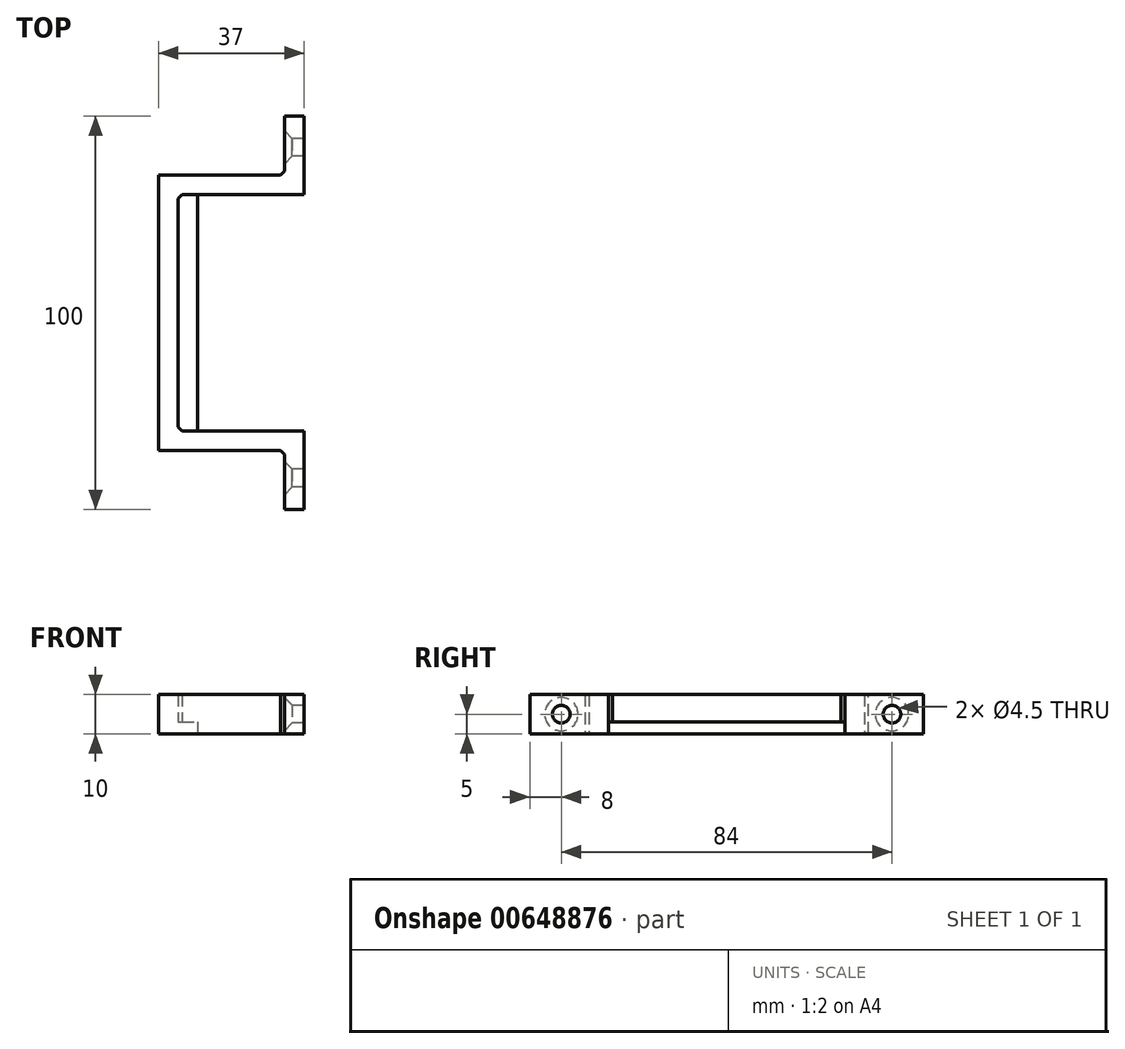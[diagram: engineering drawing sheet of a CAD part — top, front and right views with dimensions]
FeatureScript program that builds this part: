
annotation { "Feature Type Name" : "Feature", "Feature Type Description" : "" }
export const myFeature = defineFeature(function(context is Context, id is Id, definition is map)
    precondition{}
    {
        {
            var Q0;
            Q0=qCreatedBy(makeId("Top.planeOp"),FACE);
            var sketch = newSketch(context, id + "F0", { "sketchPlane" : qUnion([Q0])});
            skLineSegment(sketch, "E0", {"start": v(-30.24, 0) * mm, "end": v(66.75, 0) * mm, "construction": true});
            skLineSegment(sketch, "E1", {"start": v(0, 0) * mm, "end": v(0, 30) * mm});
            skLineSegment(sketch, "E2", {"start": v(0, 30) * mm, "end": v(32, 30) * mm});
            skLineSegment(sketch, "E3", {"start": v(32, 30) * mm, "end": v(32, 50) * mm});
            skLineSegment(sketch, "E4", {"start": v(32, 50) * mm, "end": v(27, 50) * mm});
            skLineSegment(sketch, "E5", {"start": v(27, 50) * mm, "end": v(27, 35) * mm});
            skLineSegment(sketch, "E6", {"start": v(27, 35) * mm, "end": v(-5, 35) * mm});
            skLineSegment(sketch, "E7", {"start": v(-5, 35) * mm, "end": v(-5, 0) * mm});
            skLineSegment(sketch, "E8.MirrorCS", {"start": v(-5, -35) * mm, "end": v(-5, 0) * mm});
            skLineSegment(sketch, "E9.MirrorCS", {"start": v(0, 0) * mm, "end": v(0, -30) * mm});
            skLineSegment(sketch, "E10.MirrorCS", {"start": v(27, -35) * mm, "end": v(-5, -35) * mm});
            skLineSegment(sketch, "E11.MirrorCS", {"start": v(0, -30) * mm, "end": v(32, -30) * mm});
            skLineSegment(sketch, "E12.MirrorCS", {"start": v(27, -50) * mm, "end": v(27, -35) * mm});
            skLineSegment(sketch, "E13.MirrorCS", {"start": v(32, -30) * mm, "end": v(32, -50) * mm});
            skLineSegment(sketch, "E14.MirrorCS", {"start": v(32, -50) * mm, "end": v(27, -50) * mm});
            skLineSegment(sketch, "E15", {"start": v(5, 30) * mm, "end": v(5, -30) * mm});
            skSolve(sketch);
        }
        {
            var Q0;
            {var subQ0=sQuery(id+"F0.wireOp",EDGE,"E3");Q0=makeQuery(id+"F0.imprint","IMPRINT",FACE,{"disambiguationData":[TD([[makeQuery(id+"F0.imprint","IMPRINT",EDGE,{"derivedFrom":subQ0}),1.0]])]});}
            extrude(context, id + "F1", {"entities" : qUnion([Q0]), "depth" : 10 * mm, "offsetDistance" : 25 * mm});
        }
        {
            var Q0;
            Q0=makeQuery(id+"F1.opExtrude","SWEPT_EDGE",EDGE,{"disambiguationData":[OSD([sQuery(id+"F0.wireOp",EDGE,"E9.MirrorCS"),sQuery(id+"F0.wireOp",EDGE,"E11.MirrorCS")])]});
            var Q1;
            Q1=makeQuery(id+"F1.opExtrude","SWEPT_EDGE",EDGE,{"disambiguationData":[OSD([sQuery(id+"F0.wireOp",EDGE,"E10.MirrorCS"),sQuery(id+"F0.wireOp",EDGE,"E12.MirrorCS")])]});
            var Q2;
            Q2=makeQuery(id+"F1.opExtrude","SWEPT_EDGE",EDGE,{"disambiguationData":[OSD([sQuery(id+"F0.wireOp",EDGE,"E1"),sQuery(id+"F0.wireOp",EDGE,"E2")])]});
            var Q3;
            Q3=makeQuery(id+"F1.opExtrude","SWEPT_EDGE",EDGE,{"disambiguationData":[OSD([sQuery(id+"F0.wireOp",EDGE,"E5"),sQuery(id+"F0.wireOp",EDGE,"E6")])]});
            chamfer(context, id + "F2", {"entities" : qUnion([Q0, Q1, Q2, Q3]), "width" : 1 * mm, "tangentPropagation" : true});
        }
        {
            var Q0;
            Q0=makeQuery(id+"F1.opExtrude","SWEPT_FACE",FACE,{"disambiguationData":[OSD([sQuery(id+"F0.wireOp",EDGE,"E12.MirrorCS")])]});
            cPlane(context, id + "F3", {"entities" : qUnion([Q0]), "cplaneType" : CPlaneType.OFFSET, "offset" : 0 * mm, "width" : 150 * mm, "height" : 150 * mm});
        }
        {
            var Q0;
            Q0=qCreatedBy(id+"F3.planeOp",FACE);
            var sketch = newSketch(context, id + "F4", { "sketchPlane" : qUnion([Q0])});
            skLineSegment(sketch, "E16", {"start": v(55.78, 5) * mm, "end": v(-61.85, 5) * mm, "construction": true});
            skPoint(sketch, "E17", {"position": v(42, 5) * mm});
            skPoint(sketch, "E18", {"position": v(-42, 5) * mm});
            skSolve(sketch);
        }
        {
            var Q0;
            Q0=sQuery(id+"F4.wireOp",VERTEX,"E17");
            var Q1;
            Q1=sQuery(id+"F4.wireOp",VERTEX,"E18");
            var Q2;
            Q2=makeQuery(id+"F1.opExtrude","SWEPT_BODY",BODY,{"disambiguationData":[OSD([sQuery(id+"F0.wireOp",EDGE,"E1"),sQuery(id+"F0.wireOp",EDGE,"E2"),sQuery(id+"F0.wireOp",EDGE,"E3"),sQuery(id+"F0.wireOp",EDGE,"E4"),sQuery(id+"F0.wireOp",EDGE,"E5"),sQuery(id+"F0.wireOp",EDGE,"E6"),sQuery(id+"F0.wireOp",EDGE,"E7"),sQuery(id+"F0.wireOp",EDGE,"E8.MirrorCS"),sQuery(id+"F0.wireOp",EDGE,"E9.MirrorCS"),sQuery(id+"F0.wireOp",EDGE,"E10.MirrorCS"),sQuery(id+"F0.wireOp",EDGE,"E11.MirrorCS"),sQuery(id+"F0.wireOp",EDGE,"E12.MirrorCS"),sQuery(id+"F0.wireOp",EDGE,"E13.MirrorCS"),sQuery(id+"F0.wireOp",EDGE,"E14.MirrorCS")])]});
            hole(context, id + "F5", {"style" : HoleStyle.C_SINK, "endStyle" : HoleEndStyle.THROUGH, "holeDiameter" : 4.5 * mm, "cSinkDiameter" : 8.5 * mm, "cSinkAngle" : 90 * degree, "majorDiameter" : 5 * mm, "isTappedThrough" : true, "tappedDepth" : 12 * mm, "tapClearance" : 3, "startFromSketch" : true, "locations" : qUnion([Q0, Q1]), "scope" : qUnion([Q2])});
        }
        {
            var Q0;
            {var subQ3=sQuery(id+"F0.wireOp",EDGE,"E1");Q0=makeQuery(id+"F0.imprint","IMPRINT",FACE,{"disambiguationData":[TD([[makeQuery(id+"F0.imprint","IMPRINT",EDGE,{"derivedFrom":subQ3}),-1.0]])]});}
            extrude(context, id + "F6", {"entities" : qUnion([Q0]), "operationType" : NewBodyOperationType.ADD, "depth" : 3 * mm, "offsetDistance" : 25 * mm});
        }
    });
